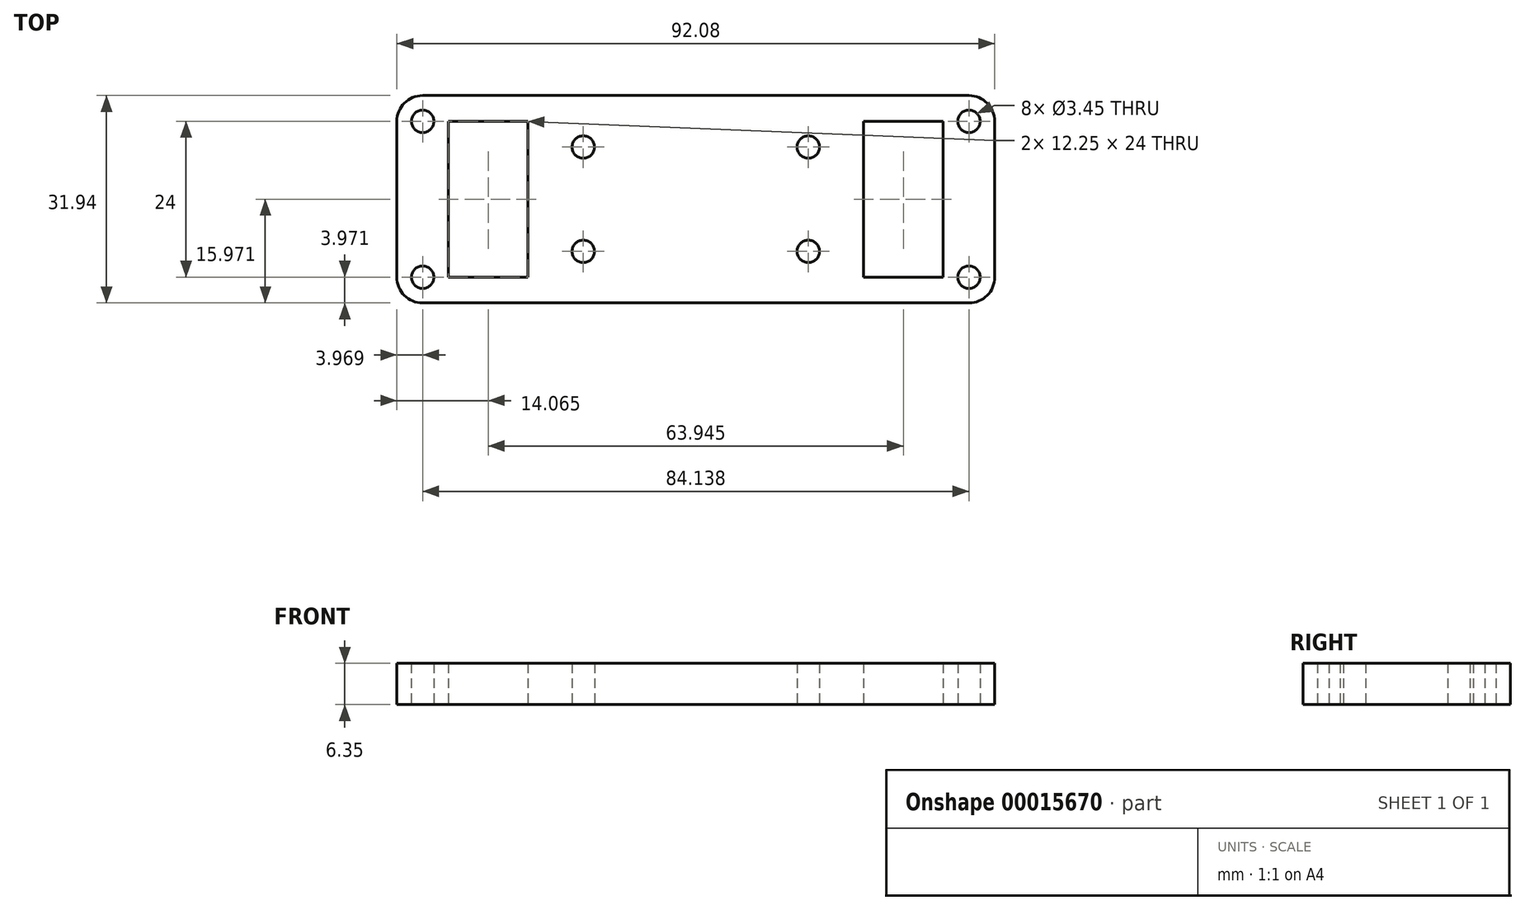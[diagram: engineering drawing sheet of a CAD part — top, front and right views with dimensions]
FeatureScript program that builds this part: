
annotation { "Feature Type Name" : "Feature", "Feature Type Description" : "" }
export const myFeature = defineFeature(function(context is Context, id is Id, definition is map)
    precondition{}
    {
        {
            var Q0;
            Q0=qCreatedBy(makeId("Top.planeOp"),FACE);
            var sketch = newSketch(context, id + "F0", { "sketchPlane" : qUnion([Q0])});
            skLineSegment(sketch, "E0.bottom", {"start": v(0, 0) * mm, "end": v(92.07, 0) * mm});
            skLineSegment(sketch, "E1.bottom", {"start": v(71.88, -3.97) * mm, "end": v(84.14, -3.97) * mm});
            skLineSegment(sketch, "E1.top", {"start": v(71.88, -27.97) * mm, "end": v(84.14, -27.97) * mm});
            skLineSegment(sketch, "E1.left", {"start": v(71.88, -3.97) * mm, "end": v(71.88, -27.97) * mm});
            skLineSegment(sketch, "E1.right", {"start": v(84.14, -3.97) * mm, "end": v(84.14, -27.97) * mm});
            skLineSegment(sketch, "E2", {"start": v(71.88, -3.97) * mm, "end": v(63.37, -3.97) * mm, "construction": true});
            skLineSegment(sketch, "E3", {"start": v(63.37, -3.97) * mm, "end": v(63.37, -7.94) * mm, "construction": true});
            skLineSegment(sketch, "E4", {"start": v(71.88, -27.97) * mm, "end": v(63.37, -27.97) * mm, "construction": true});
            skLineSegment(sketch, "E5", {"start": v(63.37, -27.97) * mm, "end": v(63.37, -24) * mm, "construction": true});
            skCircle(sketch, "E6", {"center": v(63.37, -24) * mm, "radius": 1.73 * mm});
            skCircle(sketch, "E7", {"center": v(63.37, -7.94) * mm, "radius": 1.73 * mm});
            skLineSegment(sketch, "E8", {"start": v(20.2, -3.97) * mm, "end": v(28.7, -3.97) * mm, "construction": true});
            skLineSegment(sketch, "E9", {"start": v(28.7, -3.97) * mm, "end": v(28.7, -7.94) * mm});
            skLineSegment(sketch, "E10.bottom", {"start": v(7.94, -3.97) * mm, "end": v(20.2, -3.97) * mm});
            skLineSegment(sketch, "E10.top", {"start": v(7.94, -27.97) * mm, "end": v(20.2, -27.97) * mm});
            skLineSegment(sketch, "E10.left", {"start": v(7.94, -3.97) * mm, "end": v(7.94, -27.97) * mm});
            skLineSegment(sketch, "E10.right", {"start": v(20.2, -3.97) * mm, "end": v(20.2, -27.97) * mm});
            skLineSegment(sketch, "E11", {"start": v(20.2, -27.97) * mm, "end": v(28.7, -27.97) * mm, "construction": true});
            skLineSegment(sketch, "E12", {"start": v(28.7, -27.97) * mm, "end": v(28.7, -24) * mm});
            skCircle(sketch, "E13", {"center": v(28.7, -7.94) * mm, "radius": 1.73 * mm});
            skCircle(sketch, "E14", {"center": v(28.7, -24) * mm, "radius": 1.73 * mm});
            skLineSegment(sketch, "E15", {"start": v(92.07, 0) * mm, "end": v(92.07, -31.94) * mm});
            skLineSegment(sketch, "E16", {"start": v(92.07, -31.94) * mm, "end": v(0, -31.94) * mm});
            skLineSegment(sketch, "E17", {"start": v(0, 0) * mm, "end": v(0, -31.94) * mm});
            skLineSegment(sketch, "E18", {"start": v(28.7, -27.97) * mm, "end": v(28.7, -31.94) * mm, "construction": true});
            skCircle(sketch, "E19", {"center": v(88.1, -3.97) * mm, "radius": 1.73 * mm});
            skCircle(sketch, "E20", {"center": v(3.97, -3.97) * mm, "radius": 1.73 * mm});
            skCircle(sketch, "E21", {"center": v(3.97, -27.97) * mm, "radius": 1.73 * mm});
            skCircle(sketch, "E22", {"center": v(88.1, -27.97) * mm, "radius": 1.73 * mm});
            skLineSegment(sketch, "E23", {"start": v(3.97, -3.97) * mm, "end": v(0, -3.97) * mm});
            skLineSegment(sketch, "E24", {"start": v(3.97, -27.97) * mm, "end": v(0, -27.97) * mm});
            skLineSegment(sketch, "E25", {"start": v(88.1, -3.97) * mm, "end": v(88.1, 0) * mm});
            skLineSegment(sketch, "E26", {"start": v(88.1, -3.97) * mm, "end": v(92.07, -3.97) * mm});
            skLineSegment(sketch, "E27", {"start": v(88.1, -27.97) * mm, "end": v(92.07, -27.97) * mm});
            skLineSegment(sketch, "E28", {"start": v(88.1, -27.97) * mm, "end": v(88.1, -31.94) * mm});
            skLineSegment(sketch, "E29", {"start": v(0, -15.97) * mm, "end": v(7.94, -15.97) * mm});
            skLineSegment(sketch, "E30", {"start": v(84.14, -15.97) * mm, "end": v(92.07, -15.97) * mm});
            skPoint(sketch, "E31", {"position": v(14.06, -3.97) * mm});
            skSolve(sketch);
        }
        {
            var Q0;
            Q0=qSketchRegion(id+"F0",true);
            extrude(context, id + "F1", {"entities" : qUnion([Q0]), "depth" : 6.35 * mm});
        }
        {
            var Q0;
            Q0=makeQuery(id+"F1.opExtrude","SWEPT_EDGE",EDGE,{"disambiguationData":[OSD([sQuery(id+"F0.wireOp",EDGE,"E16"),sQuery(id+"F0.wireOp",EDGE,"E17")])]});
            var Q1;
            Q1=makeQuery(id+"F1.opExtrude","SWEPT_EDGE",EDGE,{"disambiguationData":[OSD([sQuery(id+"F0.wireOp",EDGE,"E15"),sQuery(id+"F0.wireOp",EDGE,"E16")])]});
            var Q2;
            Q2=makeQuery(id+"F1.opExtrude","SWEPT_EDGE",EDGE,{"disambiguationData":[OSD([sQuery(id+"F0.wireOp",EDGE,"E0.bottom"),sQuery(id+"F0.wireOp",EDGE,"E15")])]});
            var Q3;
            Q3=makeQuery(id+"F1.opExtrude","SWEPT_EDGE",EDGE,{"disambiguationData":[OSD([sQuery(id+"F0.wireOp",EDGE,"E0.bottom"),sQuery(id+"F0.wireOp",EDGE,"E17")])]});
            fillet(context, id + "F2", {"entities" : qUnion([Q0, Q1, Q2, Q3]), "radius" : 3.97 * mm, "tangentPropagation" : true, "allowEdgeOverflow" : false});
        }
    });
